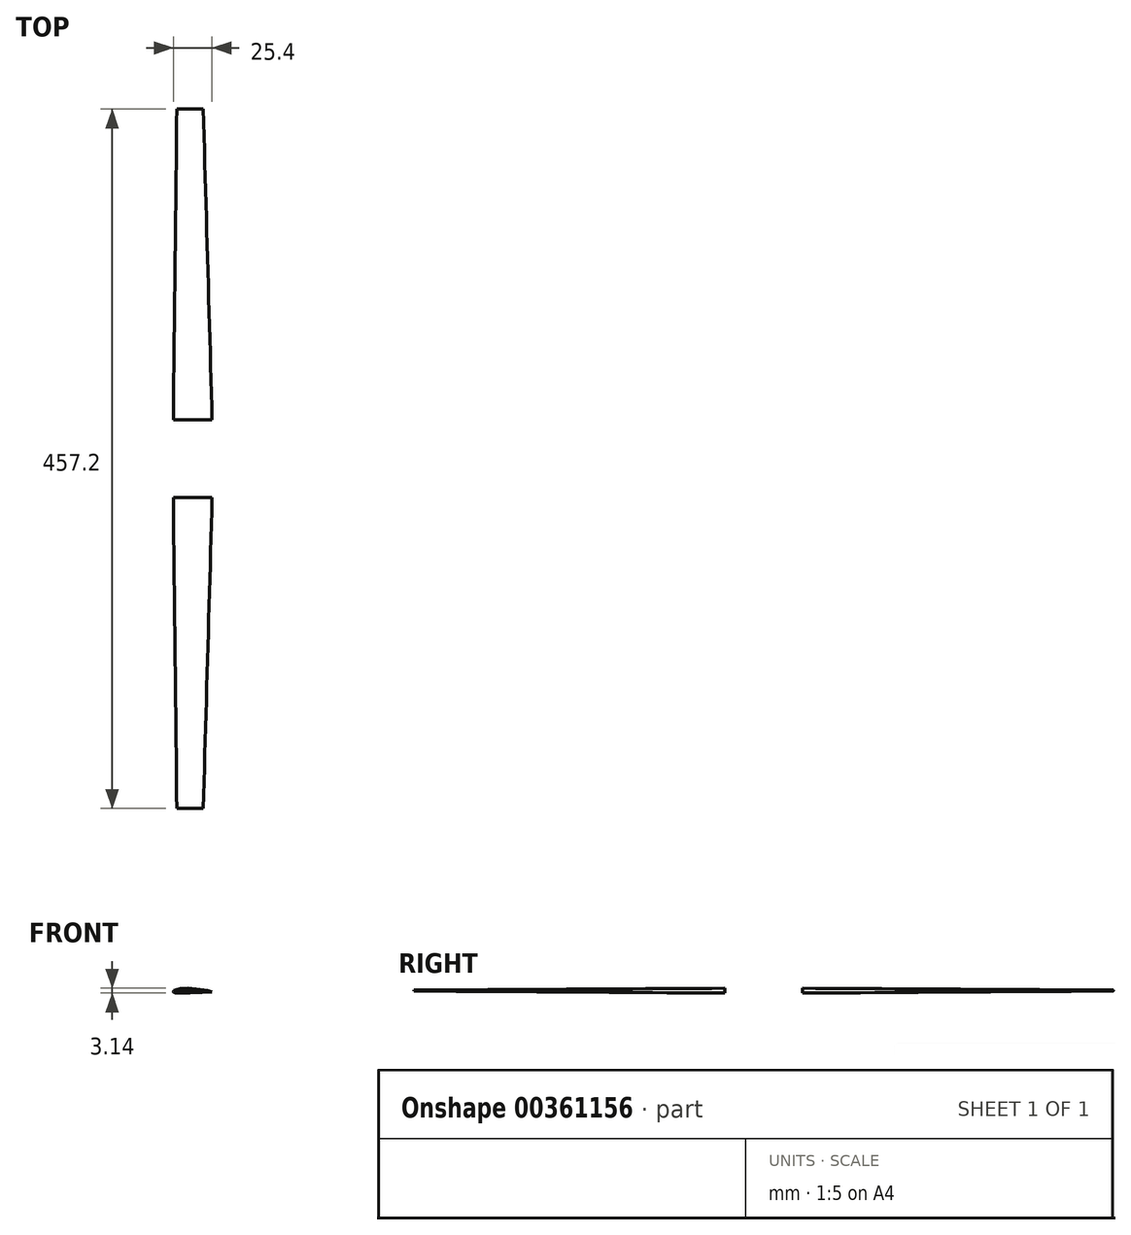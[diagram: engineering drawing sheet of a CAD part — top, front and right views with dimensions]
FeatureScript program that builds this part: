
annotation { "Feature Type Name" : "Feature", "Feature Type Description" : "" }
export const myFeature = defineFeature(function(context is Context, id is Id, definition is map)
    precondition{}
    {
        {
            var Q0;
            Q0=qCreatedBy(makeId("Front.planeOp"),FACE);
            var sketch = newSketch(context, id + "F0", { "sketchPlane" : qUnion([Q0])});
            skLineSegment(sketch, "E0", {"start": v(-20.12, 26.67) * mm, "end": v(5.28, 26.67) * mm});
            skPoint(sketch, "E1", {"position": v(4.67, 26.85) * mm});
            skPoint(sketch, "E2", {"position": v(2.88, 27.25) * mm});
            skLineSegment(sketch, "E3", {"start": v(-20.12, 26.67) * mm, "end": v(-20.12, 38.87) * mm});
            skPoint(sketch, "E4", {"position": v(0.09, 27.79) * mm});
            skPoint(sketch, "E5", {"position": v(-3.45, 28.34) * mm});
            skPoint(sketch, "E6", {"position": v(-7.4, 28.76) * mm});
            skPoint(sketch, "E7", {"position": v(-11.38, 28.93) * mm});
            skPoint(sketch, "E8", {"position": v(-15, 28.72) * mm});
            skPoint(sketch, "E9", {"position": v(-17.83, 28.15) * mm});
            skPoint(sketch, "E10", {"position": v(-19.6, 27.41) * mm});
            skPoint(sketch, "E11", {"position": v(-19.4, 26.11) * mm});
            skPoint(sketch, "E12", {"position": v(-17.56, 25.83) * mm});
            skPoint(sketch, "E13", {"position": v(-14.78, 25.8) * mm});
            skPoint(sketch, "E14", {"position": v(-11.31, 25.9) * mm});
            skPoint(sketch, "E15", {"position": v(-7.44, 26.07) * mm});
            skPoint(sketch, "E16", {"position": v(-3.54, 26.26) * mm});
            skPoint(sketch, "E17", {"position": v(0, 26.42) * mm});
            skPoint(sketch, "E18", {"position": v(2.82, 26.54) * mm});
            skFitSpline(sketch, "E19", {"points": [v(5.28, 26.67) * mm, v(4.67, 26.85) * mm, v(2.88, 27.25) * mm, v(0.09, 27.79) * mm, v(-3.45, 28.34) * mm, v(-7.4, 28.76) * mm, v(-11.38, 28.93) * mm, v(-15, 28.72) * mm, v(-17.83, 28.15) * mm, v(-19.6, 27.41) * mm, v(-20.12, 26.67) * mm, v(-19.4, 26.11) * mm, v(-17.56, 25.83) * mm, v(-14.78, 25.8) * mm, v(-11.31, 25.9) * mm, v(-7.44, 26.07) * mm, v(-3.54, 26.26) * mm, v(0, 26.42) * mm, v(2.82, 26.54) * mm, v(5.28, 26.67) * mm]});
            skSolve(sketch);
        }
        {
            var Q0;
            Q0=qCreatedBy(makeId("Front.planeOp"),FACE);
            cPlane(context, id + "F1", {"entities" : qUnion([Q0]), "cplaneType" : CPlaneType.OFFSET, "offset" : 203.2 * mm, "width" : 152.4 * mm, "height" : 152.4 * mm});
        }
        {
            var Q0;
            Q0=qCreatedBy(id+"F1.planeOp",FACE);
            var sketch = newSketch(context, id + "F2", { "sketchPlane" : qUnion([Q0])});
            skEllipse(sketch, "E20", {"center": v(-9.17, 27.44) * mm, "majorRadius": 8.64 * mm, "minorRadius": 0.27 * mm, "majorAxis": v(-1, 0)});
            skSolve(sketch);
        }
        {
            var Q0;
            Q0=sQuery(id+"F0.wireOp",EDGE,"E19");
            var Q1;
            Q1=sQuery(id+"F2.wireOp",EDGE,"E20");
            loft(context, id + "F3", {"bodyType" : ToolBodyType.SURFACE, "wireProfilesArray" : [{ "wireProfileEntities" : qUnion([Q0]) }, { "wireProfileEntities" : qUnion([Q1]) }]});
        }
        {
            var Q0;
            Q0=qCreatedBy(makeId("Front.planeOp"),FACE);
            cPlane(context, id + "F4", {"entities" : qUnion([Q0]), "cplaneType" : CPlaneType.OFFSET, "offset" : 25.4 * mm, "oppositeDirection" : true, "width" : 152.4 * mm, "height" : 152.4 * mm});
        }
        {
            var Q0;
            Q0=makeQuery(id+"F3.opLoft","SWEPT_BODY",BODY,{"disambiguationData":[OSD([sQuery(id+"F0.wireOp",EDGE,"E19"),sQuery(id+"F2.wireOp",EDGE,"E20")])]});
            var Q1;
            Q1=qCreatedBy(id+"F4.planeOp",FACE);
            mirror(context, id + "F5", {"entities" : qUnion([Q0]), "mirrorPlane" : qUnion([Q1])});
        }
    });
